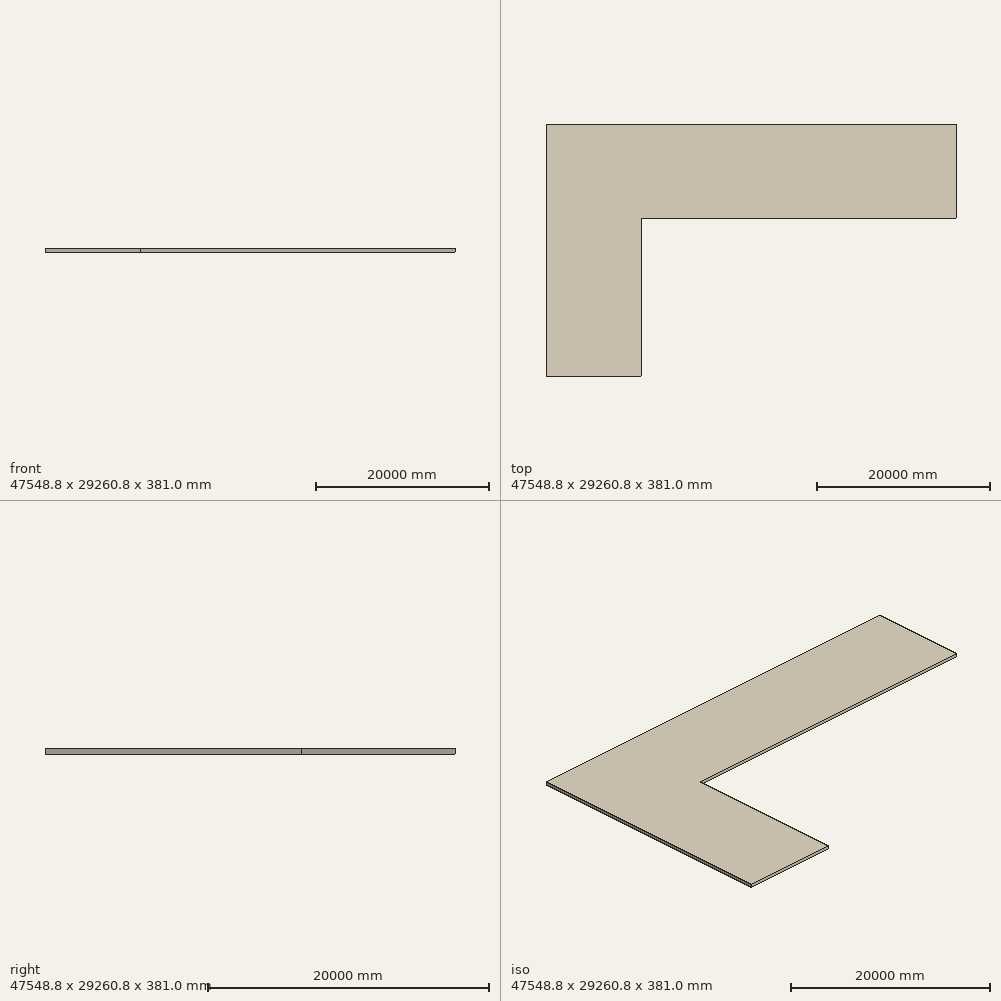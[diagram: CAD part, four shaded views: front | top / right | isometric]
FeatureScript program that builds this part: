
annotation { "Feature Type Name" : "Feature", "Feature Type Description" : "" }
export const myFeature = defineFeature(function(context is Context, id is Id, definition is map)
    precondition{}
    {
        {
            var Q0;
            Q0=qCreatedBy(makeId("Top.planeOp"),FACE);
            var sketch = newSketch(context, id + "F0", { "sketchPlane" : qUnion([Q0])});
            skLineSegment(sketch, "E0", {"start": v(-914.4, 914.4) * mm, "end": v(46634.4, 914.4) * mm});
            skLineSegment(sketch, "E1", {"start": v(46634.4, 914.4) * mm, "end": v(46634.4, -10058.4) * mm});
            skLineSegment(sketch, "E2", {"start": v(46634.4, -10058.4) * mm, "end": v(10058.4, -10058.4) * mm});
            skLineSegment(sketch, "E3", {"start": v(10058.4, -10058.4) * mm, "end": v(10058.4, -28346.4) * mm});
            skLineSegment(sketch, "E4", {"start": v(10058.4, -28346.4) * mm, "end": v(-914.4, -28346.4) * mm});
            skLineSegment(sketch, "E5", {"start": v(-914.4, -28346.4) * mm, "end": v(-914.4, 914.4) * mm});
            skSolve(sketch);
        }
        {
            var Q0;
            Q0=makeQuery(id+"F0.imprint","IMPRINT",FACE,{"disambiguationData":[TD([[makeQuery(id+"F0.imprint","IMPRINT",EDGE,{"derivedFrom":sQuery(id+"F0.wireOp",EDGE,"E0")}),-1.0]])]});
            extrude(context, id + "F1", {"entities" : qUnion([Q0]), "oppositeDirection" : true, "depth" : 381 * mm, "offsetDistance" : 30.48 * mm});
        }
    });
